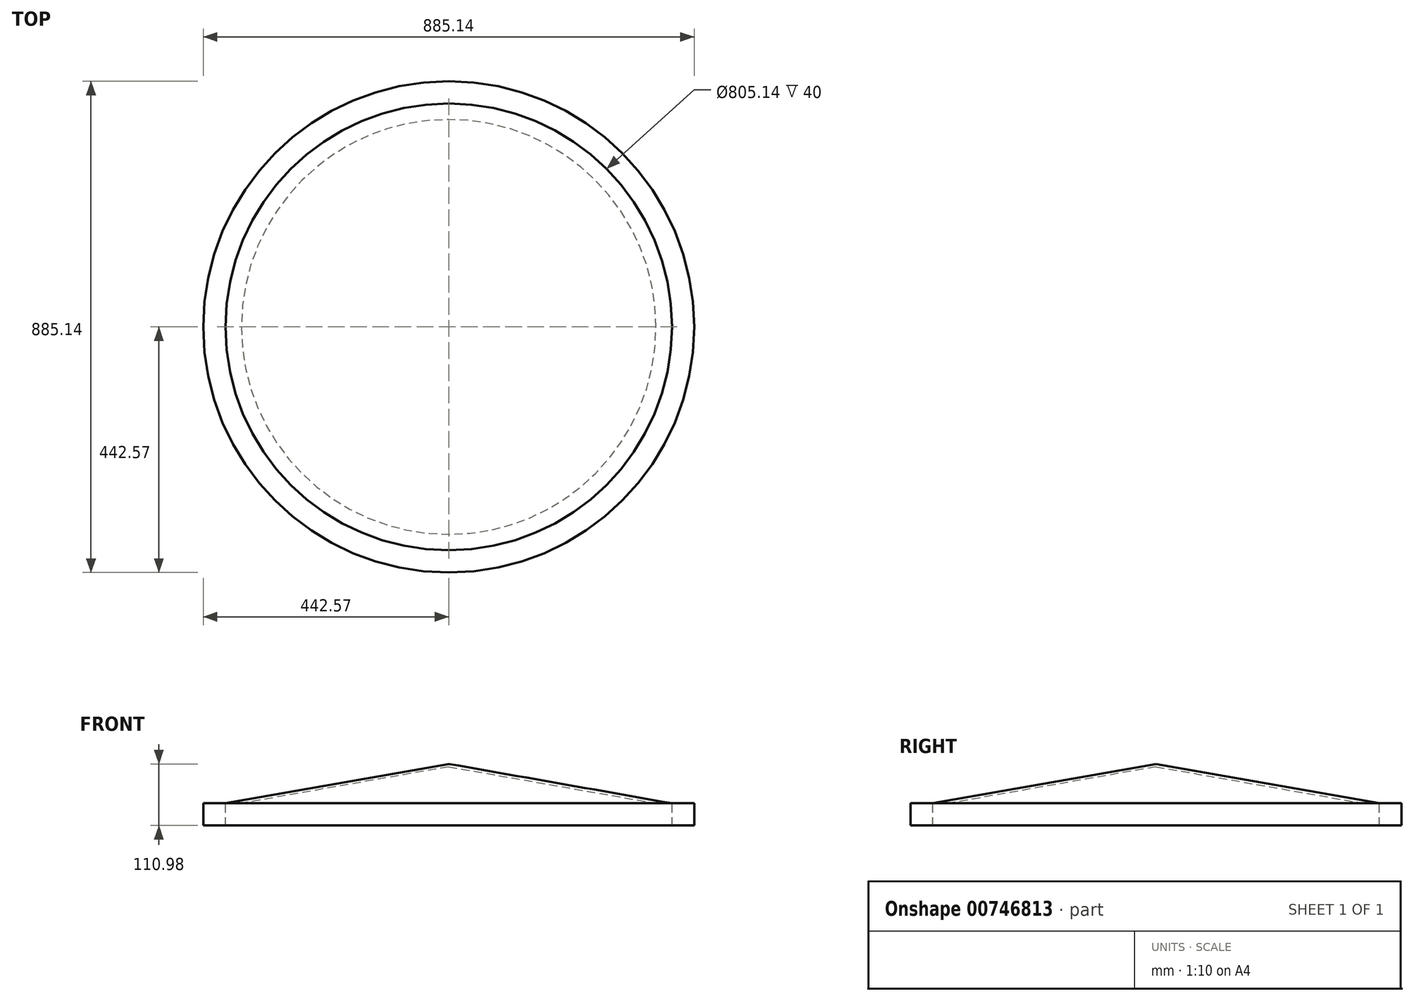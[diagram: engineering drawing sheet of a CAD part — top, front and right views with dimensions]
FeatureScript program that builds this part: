
annotation { "Feature Type Name" : "Feature", "Feature Type Description" : "" }
export const myFeature = defineFeature(function(context is Context, id is Id, definition is map)
    precondition{}
    {
        {
            var Q0;
            Q0=qCreatedBy(makeId("Top.planeOp"),FACE);
            var sketch = newSketch(context, id + "F0", { "sketchPlane" : qUnion([Q0])});
            skCircle(sketch, "E0", {"center": v(0, 0) * mm, "radius": 442.57 * mm});
            skSolve(sketch);
        }
        {
            var Q0;
            Q0=qSketchRegion(id+"F0",true);
            extrude(context, id + "F1", {"entities" : qUnion([Q0]), "depth" : 40 * mm, "offsetDistance" : 25.4 * mm});
        }
        {
            var Q0;
            Q0=makeQuery(id+"F1.opExtrude","CAP_FACE",FACE,{"disambiguationData":[OSD([sQuery(id+"F0.wireOp",EDGE,"E0")])],"isStart":false});
            var sketch = newSketch(context, id + "F2", { "sketchPlane" : qUnion([Q0])});
            skCircle(sketch, "E1", {"center": v(0, 0) * mm, "radius": 402.57 * mm});
            skSolve(sketch);
        }
        {
            var Q0;
            Q0=qSketchRegion(id+"F2",true);
            extrude(context, id + "F3", {"entities" : qUnion([Q0]), "operationType" : NewBodyOperationType.REMOVE, "oppositeDirection" : true, "depth" : 93.98 * mm, "offsetDistance" : 25.4 * mm});
        }
        {
            var Q0;
            Q0=makeQuery(id+"F1.opExtrude","CAP_FACE",FACE,{"disambiguationData":[OSD([sQuery(id+"F0.wireOp",EDGE,"E0")])],"isStart":false});
            var sketch = newSketch(context, id + "F4", { "sketchPlane" : qUnion([Q0])});
            skCircle(sketch, "E2", {"center": v(0, 0) * mm, "radius": 402.57 * mm});
            skSolve(sketch);
        }
        {
            var Q0;
            Q0=qSketchRegion(id+"F4",true);
            extrude(context, id + "F5", {"entities" : qUnion([Q0]), "depth" : 100 * mm, "offsetDistance" : 25.4 * mm, "hasDraft" : true, "draftAngle" : 80 * degree, "draftPullDirection" : true});
        }
        {
            var Q0;
            Q0=makeQuery(id+"F5.opExtrude","CAP_FACE",FACE,{"disambiguationData":[OSD([sQuery(id+"F4.wireOp",EDGE,"E2")])],"isStart":true});
            shell(context, id + "F6", {"entities" : qUnion([Q0]), "thickness" : 5 * mm});
        }
    });
